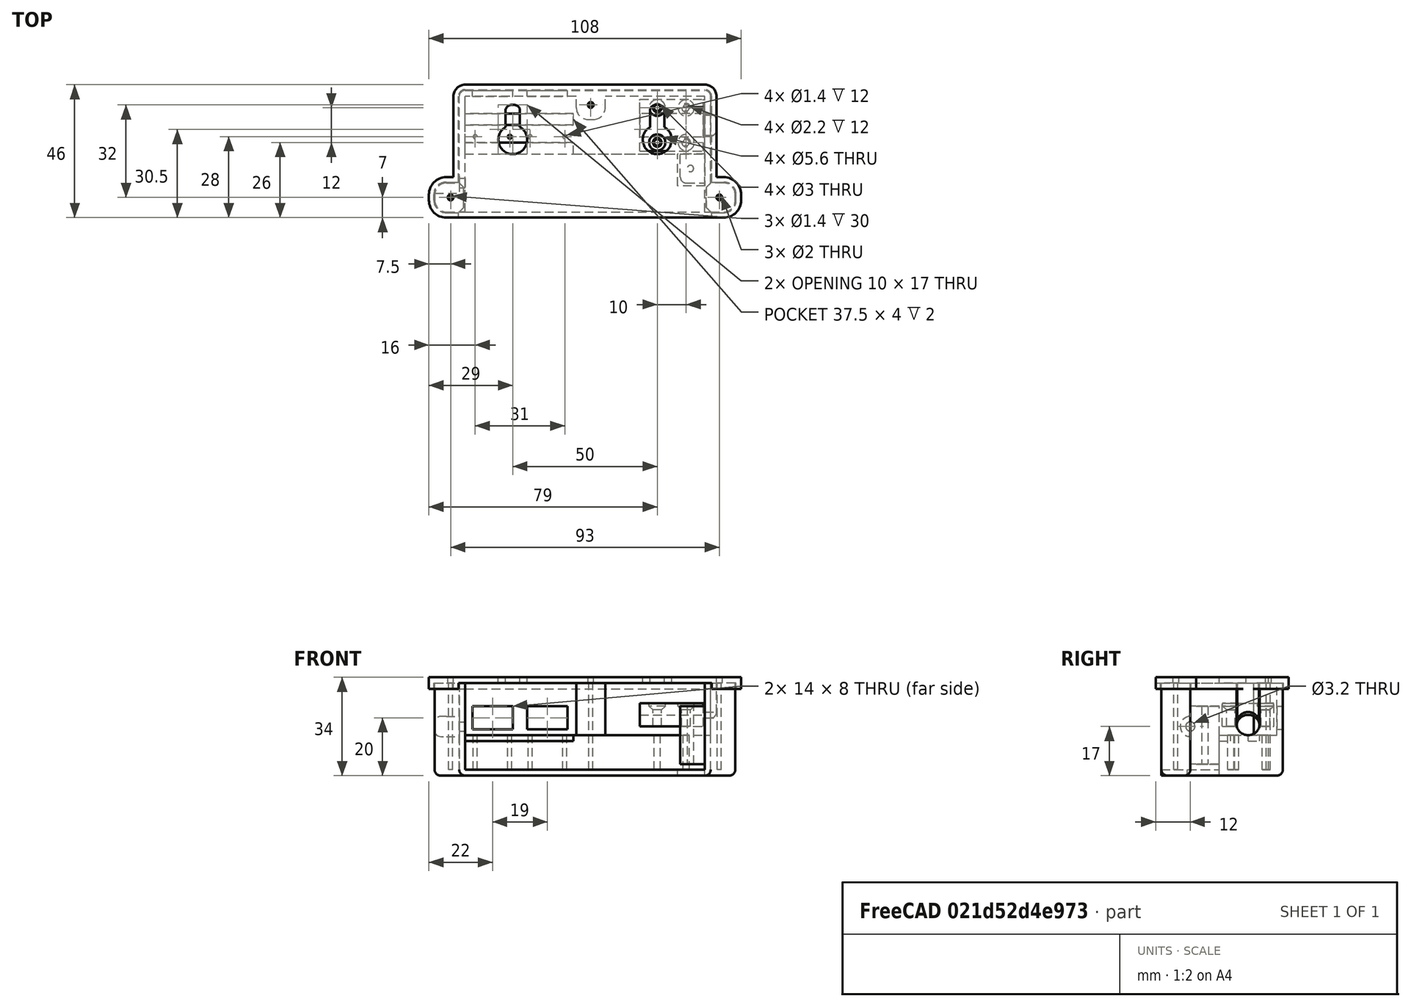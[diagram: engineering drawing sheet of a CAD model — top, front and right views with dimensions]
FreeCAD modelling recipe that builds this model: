
FCSTD DOCUMENT  (FreeCAD 0.19R)
Label: PwrCap5V7A
License: All rights reserved
LicenseURL: https://en.wikipedia.org/wiki/All_rights_reserved
objects: Part::Cylinder×27, Part::Box×23, Part::Fillet×18, Part::MultiFuse×12, Part::Cut×7, Part::Chamfer×4, Part::Feature×1
note: 92 computed .brp shape members not serialized (recipe doc carries the construction recipe); baked Part::Feature solids carry a one-line shape summary decoded from their .brp

FEATURE [Part::Box] Box  label="Hollow001"
  AttacherType = Attacher::AttachEngine3D
  Height = 12
  Length = 83
  Placement = pos=(-41.5,20,2) rot=(0,0,1;0rad)
  Width = 20
FEATURE [Part::Box] Box001  label="BoxCube"
  AttacherType = Attacher::AttachEngine3D
  Height = 32
  Length = 87
  Placement = pos=(-43.5,0,0) rot=(0,0,1;0rad)
  Width = 42
FEATURE [Part::Box] Box002  label="Hollow002"
  AttacherType = Attacher::AttachEngine3D
  Height = 40
  Length = 83
  Placement = pos=(-41.5,0,2) rot=(0,0,1;0rad)
  Width = 40
FEATURE [Part::Box] Box003  label="Cube"
  AttacherType = Attacher::AttachEngine3D
  Height = 32
  Length = 10
  Placement = pos=(-3,32,0) rot=(0,0,1;0rad)
  Width = 10
FEATURE [Part::MultiFuse] Fusion
  Shapes = -> [Box,Box003]
FEATURE [Part::Fillet] Fillet
  Base = -> Fusion
  Edges = 2 edges r=4: [Edge23,Edge27]
FEATURE [Part::Cut] Cut
  Base = -> Box002
  Tool = -> Fillet
FEATURE [Part::Box] Box004  label="Cube002"
  AttacherType = Attacher::AttachEngine3D
  Height = 32
  Length = 10
  Placement = pos=(-52,0,0) rot=(0,0,1;0rad)
  Width = 10
FEATURE [Part::Fillet] Fillet001  label="ScrewHolder002"
  Base = -> Box004
  Edges = 2 edges r=4: [Edge1,Edge3]
FEATURE [Part::Box] Box005  label="Cube003"
  AttacherType = Attacher::AttachEngine3D
  Height = 32
  Length = 10
  Placement = pos=(42,0,0) rot=(0,0,1;0rad)
  Width = 10
FEATURE [Part::Fillet] Fillet002  label="ScrewHolder001"
  Base = -> Box005
  Edges = 2 edges r=4: [Edge5,Edge7]
FEATURE [Part::Cylinder] Cylinder  label="ScreHolle001"
  Angle = 360
  AttacherType = Attacher::AttachEngine3D
  Height = 20
  Placement = pos=(-55,10,17) rot=(0,1,0;1.5708rad)
  Radius = 1.6
FEATURE [Part::Cylinder] Cylinder001  label="ScreHolle002"
  Angle = 360
  AttacherType = Attacher::AttachEngine3D
  Height = 30
  Placement = pos=(36.5,15,0) rot=(0,0,1;0rad)
  Radius = 1.1
FEATURE [Part::Cylinder] Cylinder002  label="ScreHolle003"
  Angle = 360
  AttacherType = Attacher::AttachEngine3D
  Height = 40
  Placement = pos=(2,37,2) rot=(0,0,1;0rad)
  Radius = 0.7
FEATURE [Part::Cylinder] Cylinder003  label="ScreHolle004"
  Angle = 360
  AttacherType = Attacher::AttachEngine3D
  Height = 40
  Placement = pos=(46.5,5,2) rot=(0,0,1;0rad)
  Radius = 0.7
FEATURE [Part::Cylinder] Cylinder004  label="ScreHolle005"
  Angle = 360
  AttacherType = Attacher::AttachEngine3D
  Height = 40
  Placement = pos=(-46.5,5,2) rot=(0,0,1;0rad)
  Radius = 0.7
FEATURE [Part::Cylinder] Cylinder005  label="ScreHolle006"
  Angle = 360
  AttacherType = Attacher::AttachEngine3D
  Height = 30
  Placement = pos=(35,24,2) rot=(0,0,1;0rad)
  Radius = 1.1
FEATURE [Part::Cylinder] Cylinder006  label="ScreHolle007"
  Angle = 360
  AttacherType = Attacher::AttachEngine3D
  Height = 30
  Placement = pos=(25,36,2) rot=(0,0,1;0rad)
  Radius = 1.1
FEATURE [Part::Box] Box007  label="Cube005"
  AttacherType = Attacher::AttachEngine3D
  Height = 20
  Length = 30
  Placement = pos=(20,26,14) rot=(0,0,1;0rad)
  Width = 8
FEATURE [Part::Cylinder] Cylinder007  label="ScreHolle008"
  Angle = 360
  AttacherType = Attacher::AttachEngine3D
  Height = 30
  Placement = pos=(35,36,2) rot=(0,0,1;0rad)
  Radius = 1.1
FEATURE [Part::Cylinder] Cylinder008  label="ScreHolle009"
  Angle = 360
  AttacherType = Attacher::AttachEngine3D
  Height = 30
  Placement = pos=(25,24,2) rot=(0,0,1;0rad)
  Radius = 1.1
FEATURE [Part::Fillet] Fillet003
  Base = -> Box007
  Edges = 2 edges r=3.9: [Edge9,Edge11]
FEATURE [Part::Fillet] Fillet004
  Base = -> Box001
  Edges = 2 edges r=2: [Edge3,Edge7]
FEATURE [Part::Fillet] Fillet005  label="MainBoxCube"
  Base = -> Fillet004
  Edges = 1 edges r=2: [Edge16]
FEATURE [Part::Fillet] Fillet006  label="ScrewHolder003"
  Base = -> Fillet002
  Edges = 1 edges r=2: [Edge12]
FEATURE [Part::Fillet] Fillet007  label="ScrewHolder004"
  Base = -> Fillet001
  Edges = 1 edges r=2: [Edge14]
FEATURE [Part::Cylinder] Cylinder009  label="ScreHolle010"
  Angle = 360
  AttacherType = Attacher::AttachEngine3D
  Height = 11.5
  Placement = pos=(-55,10,17) rot=(0,1,0;1.5708rad)
  Radius = 3.5
FEATURE [Part::Box] Box012  label="Cube010"
  AttacherType = Attacher::AttachEngine3D
  Height = 20
  Length = 10
  Placement = pos=(33,10,4) rot=(0,0,1;0rad)
  Width = 10
FEATURE [Part::Fillet] Fillet008  label="ScrewHolder005"
  Base = -> Box012
  Edges = 1 edges r=2: [Edge1]
FEATURE [Part::Box] Box013  label="Cube011"
  AttacherType = Attacher::AttachEngine3D
  Height = 4
  Length = 9.5
  Placement = pos=(32,9,-1) rot=(0,0,1;0rad)
  Width = 11
FEATURE [Part::MultiFuse] Fusion005003  label="BoxBody"
  Shapes = -> [Fillet007,Fillet005,Fillet006]
FEATURE [Part::Cut] Cut001
  Base = -> Cut
  Tool = -> Fillet008
FEATURE [Part::Box] Box014  label="BoxCube001"
  AttacherType = Attacher::AttachEngine3D
  Height = 2
  Length = 87.6
  Placement = pos=(-43.8,-2,0) rot=(0,0,1;0rad)
  Width = 44.3
FEATURE [Part::Box] Box015  label="Cube012"
  AttacherType = Attacher::AttachEngine3D
  Height = 2
  Length = 10.3
  Placement = pos=(-52.3,-0.3,0) rot=(0,0,1;0rad)
  Width = 10.6
FEATURE [Part::Fillet] Fillet009  label="ScrewHolder006"
  Base = -> Box015
  Edges = 2 edges r=4.3: [Edge1,Edge3]
FEATURE [Part::Box] Box016  label="Cube013"
  AttacherType = Attacher::AttachEngine3D
  Height = 2
  Length = 10.3
  Placement = pos=(42,-0.3,0) rot=(0,0,1;0rad)
  Width = 10.6
FEATURE [Part::Fillet] Fillet010  label="ScrewHolder007"
  Base = -> Box016
  Edges = 2 edges r=4.3: [Edge5,Edge7]
FEATURE [Part::Fillet] Fillet013
  Base = -> Box014
  Edges = 2 edges r=2.3: [Edge3,Edge7]
FEATURE [Part::MultiFuse] Fusion005005  label="CapHollow"
  Shapes = -> [Fillet013,Fillet009,Fillet010]
FEATURE [Part::Cylinder] Cylinder012  label="ScreHolle011"
  Angle = 360
  AttacherType = Attacher::AttachEngine3D
  Height = 5
  Placement = pos=(-46.5,5,0) rot=(0,0,1;0rad)
  Radius = 1
FEATURE [Part::Cylinder] Cylinder013  label="ScreHolle012"
  Angle = 360
  AttacherType = Attacher::AttachEngine3D
  Height = 5
  Placement = pos=(46.5,5,0) rot=(0,0,1;0rad)
  Radius = 1
FEATURE [Part::Cylinder] Cylinder014  label="ScreHolle013"
  Angle = 360
  AttacherType = Attacher::AttachEngine3D
  Height = 5
  Placement = pos=(2,37,0) rot=(0,0,1;0rad)
  Radius = 1
FEATURE [Part::MultiFuse] Fusion005006  label="CapScrews"
  Shapes = -> [Cylinder012,Cylinder013,Cylinder014]
FEATURE [Part::Cylinder] Cylinder015  label="ScreHolle014"
  Angle = 360
  AttacherType = Attacher::AttachEngine3D
  Height = 25
  Placement = pos=(35,24,2) rot=(0,0,1;0rad)
  Radius = 1.5
FEATURE [Part::Cylinder] Cylinder016  label="ScreHolle015"
  Angle = 360
  AttacherType = Attacher::AttachEngine3D
  Height = 25
  Placement = pos=(25,36,2) rot=(0,0,1;0rad)
  Radius = 1.5
FEATURE [Part::Cylinder] Cylinder017  label="ScreHolle016"
  Angle = 360
  AttacherType = Attacher::AttachEngine3D
  Height = 25
  Placement = pos=(35,36,2) rot=(0,0,1;0rad)
  Radius = 1.5
FEATURE [Part::Cylinder] Cylinder018  label="ScreHolle017"
  Angle = 360
  AttacherType = Attacher::AttachEngine3D
  Height = 25
  Placement = pos=(25,24,2) rot=(0,0,1;0rad)
  Radius = 1.5
FEATURE [Part::Box] Box017  label="CableCube"
  AttacherType = Attacher::AttachEngine3D
  Height = 8
  Length = 22
  Placement = pos=(19,21,13) rot=(0,0,1;0rad)
  Width = 18
FEATURE [Part::Box] Box018  label="Cube015"
  AttacherType = Attacher::AttachEngine3D
  Height = 5
  Length = 40
  Placement = pos=(10,26,12) rot=(0,0,1;0rad)
  Width = 8
FEATURE [Part::Fillet] Fillet014
  Base = -> Box018
  Edges = 2 edges r=3.9: [Edge10,Edge12]
FEATURE [Part::Cylinder] Cylinder019  label="ScreHolle018"
  Angle = 360
  AttacherType = Attacher::AttachEngine3D
  Height = 5
  Placement = pos=(35,24,18) rot=(0,0,1;0rad)
  Radius = 2.8
FEATURE [Part::Cylinder] Cylinder020  label="ScreHolle019"
  Angle = 360
  AttacherType = Attacher::AttachEngine3D
  Height = 5
  Placement = pos=(25,36,18) rot=(0,0,1;0rad)
  Radius = 2.8
FEATURE [Part::Cylinder] Cylinder021  label="ScreHolle020"
  Angle = 360
  AttacherType = Attacher::AttachEngine3D
  Height = 5
  Placement = pos=(35,36,18) rot=(0,0,1;0rad)
  Radius = 2.8
FEATURE [Part::Cylinder] Cylinder022  label="ScreHolle021"
  Angle = 360
  AttacherType = Attacher::AttachEngine3D
  Height = 5
  Placement = pos=(25,24,18) rot=(0,0,1;0rad)
  Radius = 2.8
FEATURE [Part::Chamfer] Chamfer
  Base = -> Cylinder022
  Edges = 1 edges r=2: [Edge3]
FEATURE [Part::Chamfer] Chamfer001
  Base = -> Cylinder020
  Edges = 1 edges r=2: [Edge3]
FEATURE [Part::Chamfer] Chamfer002
  Base = -> Cylinder021
  Edges = 1 edges r=2: [Edge3]
FEATURE [Part::Chamfer] Chamfer003
  Base = -> Cylinder019
  Edges = 1 edges r=2: [Edge3]
FEATURE [Part::MultiFuse] Fusion005007
  Shapes = -> [Chamfer,Cylinder018,Chamfer001,Cylinder016,Cylinder017,Chamfer002,Cylinder015,Chamfer003,Fillet014]
FEATURE [Part::Cut] Cut004  label="CableCap"
  Base = -> Box017
  Placement = pos=(0,0,4) rot=(0,0,1;0rad)
  Tool = -> Fusion005007
FEATURE [Part::Box] Box019  label="Cube016"
  AttacherType = Attacher::AttachEngine3D
  Height = 8
  Length = 14
  Placement = pos=(-39,35,16) rot=(0,0,1;0rad)
  Width = 14
FEATURE [Part::Box] Box020  label="Cube017"
  AttacherType = Attacher::AttachEngine3D
  Height = 8
  Length = 14
  Placement = pos=(-20,35,16) rot=(0,0,1;0rad)
  Width = 14
FEATURE [Part::Box] Box021  label="Cube018"
  AttacherType = Attacher::AttachEngine3D
  Height = 3
  Length = 37.5
  Placement = pos=(-41.5,20,12) rot=(0,0,1;0rad)
  Width = 4
FEATURE [Part::Box] Box022  label="Cube019"
  AttacherType = Attacher::AttachEngine3D
  Height = 3
  Length = 37.5
  Placement = pos=(-41.5,30,12) rot=(0,0,1;0rad)
  Width = 4
FEATURE [Part::Cylinder] Cylinder023
  Angle = 360
  AttacherType = Attacher::AttachEngine3D
  Height = 15
  Placement = pos=(-38,26,2) rot=(0,0,1;0rad)
  Radius = 0.7
FEATURE [Part::Cylinder] Cylinder024
  Angle = 360
  AttacherType = Attacher::AttachEngine3D
  Height = 15
  Placement = pos=(-26,26,2) rot=(0,0,1;0rad)
  Radius = 0.7
FEATURE [Part::Cylinder] Cylinder025
  Angle = 360
  AttacherType = Attacher::AttachEngine3D
  Height = 15
  Placement = pos=(-19,26,2) rot=(0,0,1;0rad)
  Radius = 0.7
FEATURE [Part::Cylinder] Cylinder026
  Angle = 360
  AttacherType = Attacher::AttachEngine3D
  Height = 15
  Placement = pos=(-7,26,2) rot=(0,0,1;0rad)
  Radius = 0.7
FEATURE [Part::MultiFuse] Fusion005008  label="UsbConnectorHolles"
  Shapes = -> [Cylinder026,Box019,Box020,Box021,Box022,Cylinder023,Cylinder024,Cylinder025]
FEATURE [Part::MultiFuse] Fusion005009  label="BoxHollows"
  Shapes = -> [Cut001,Fusion005008,Box013,Cylinder009,Fillet003,Cylinder008,Cylinder007,Cylinder006,Cylinder005,Cylinder004,Cylinder003,Cylinder002,Cylinder001,Cylinder]
FEATURE [Part::Cut] Cut005  label="PwrBox"
  Base = -> Fusion005003
  Tool = -> Fusion005009
FEATURE [Part::Box] Box023  label="BoxCube002"
  AttacherType = Attacher::AttachEngine3D
  Height = 4
  Length = 91
  Placement = pos=(-45.5,-2,0) rot=(0,0,1;0rad)
  Width = 46
FEATURE [Part::Box] Box024  label="Cube020"
  AttacherType = Attacher::AttachEngine3D
  Height = 4
  Length = 10
  Placement = pos=(-54,-2,0) rot=(0,0,1;0rad)
  Width = 14
FEATURE [Part::Fillet] Fillet015  label="ScrewHolder008"
  Base = -> Box024
  Edges = 2 edges r=6: [Edge1,Edge3]
FEATURE [Part::Box] Box025  label="Cube021"
  AttacherType = Attacher::AttachEngine3D
  Height = 4
  Length = 10
  Placement = pos=(44,-2,0) rot=(0,0,1;0rad)
  Width = 14
FEATURE [Part::Fillet] Fillet016  label="ScrewHolder009"
  Base = -> Box025
  Edges = 2 edges r=6: [Edge5,Edge7]
FEATURE [Part::Fillet] Fillet017
  Base = -> Box023
  Edges = 2 edges r=4: [Edge3,Edge7]
FEATURE [Part::MultiFuse] Fusion005010  label="CapCover"
  Shapes = -> [Fillet017,Fillet015,Fillet016]
FEATURE [Part::MultiFuse] Fusion005011
  Shapes = -> [Fusion005005,Fusion005006]
FEATURE [Part::Cut] Cut006  label="CoverBody"
  Base = -> Fusion005010
  Tool = -> Fusion005011
FEATURE [Part::Box] Box026  label="Cube022"
  AttacherType = Attacher::AttachEngine3D
  Height = 10
  Length = 5
  Placement = pos=(-2.5,0,0) rot=(0,0,1;0rad)
  Width = 12
FEATURE [Part::Cylinder] Cylinder027  label="Cylinder"
  Angle = 360
  AttacherType = Attacher::AttachEngine3D
  Height = 10
  Radius = 5
FEATURE [Part::Fillet] Fillet018
  Base = -> Box026
  Edges = 2 edges r=2: [Edge3,Edge7]
FEATURE [Part::MultiFuse] Fusion005012  label="HangScrewHolle1"
  Placement = pos=(25,25,0) rot=(0,0,1;0rad)
  Shapes = -> [Fillet018,Cylinder027]
FEATURE [Part::Feature] Fusion005012001  label="HangScrewHolle2"
  Placement = pos=(-25,25,0) rot=(0,0,1;0rad)
  shape: bbox 10 x 17 x 10 mm, 13 faces (baked)
FEATURE [Part::MultiFuse] Fusion005012002
  Shapes = -> [Fusion005012001,Fusion005012]
FEATURE [Part::Cut] Cut007  label="CoverPannel"
  Base = -> Cut006
  Placement = pos=(0,0,30) rot=(0,0,1;0rad)
  Tool = -> Fusion005012002
FEATURE [Part::Box] Box027  label="Cube023"
  AttacherType = Attacher::AttachEngine3D
  Height = 14
  Length = 4
  Placement = pos=(41.5,26.3,20) rot=(0,0,1;0rad)
  Width = 7.4
FEATURE [Part::Cylinder] Cylinder028
  Angle = 360
  AttacherType = Attacher::AttachEngine3D
  Height = 10
  Placement = pos=(40,30,18) rot=(0,1,0;1.5708rad)
  Radius = 4
FEATURE [Part::Fillet] Fillet019
  Base = -> Box027
  Edges = 2 edges r=2: [Edge5,Edge7]
FEATURE [Part::Cut] Cut008  label="CableCover"
  Base = -> Fillet019
  Tool = -> Cylinder028
FEATURE [Part::MultiFuse] Fusion005012003  label="Cover"
  Shapes = -> [Cut007,Cut008]
